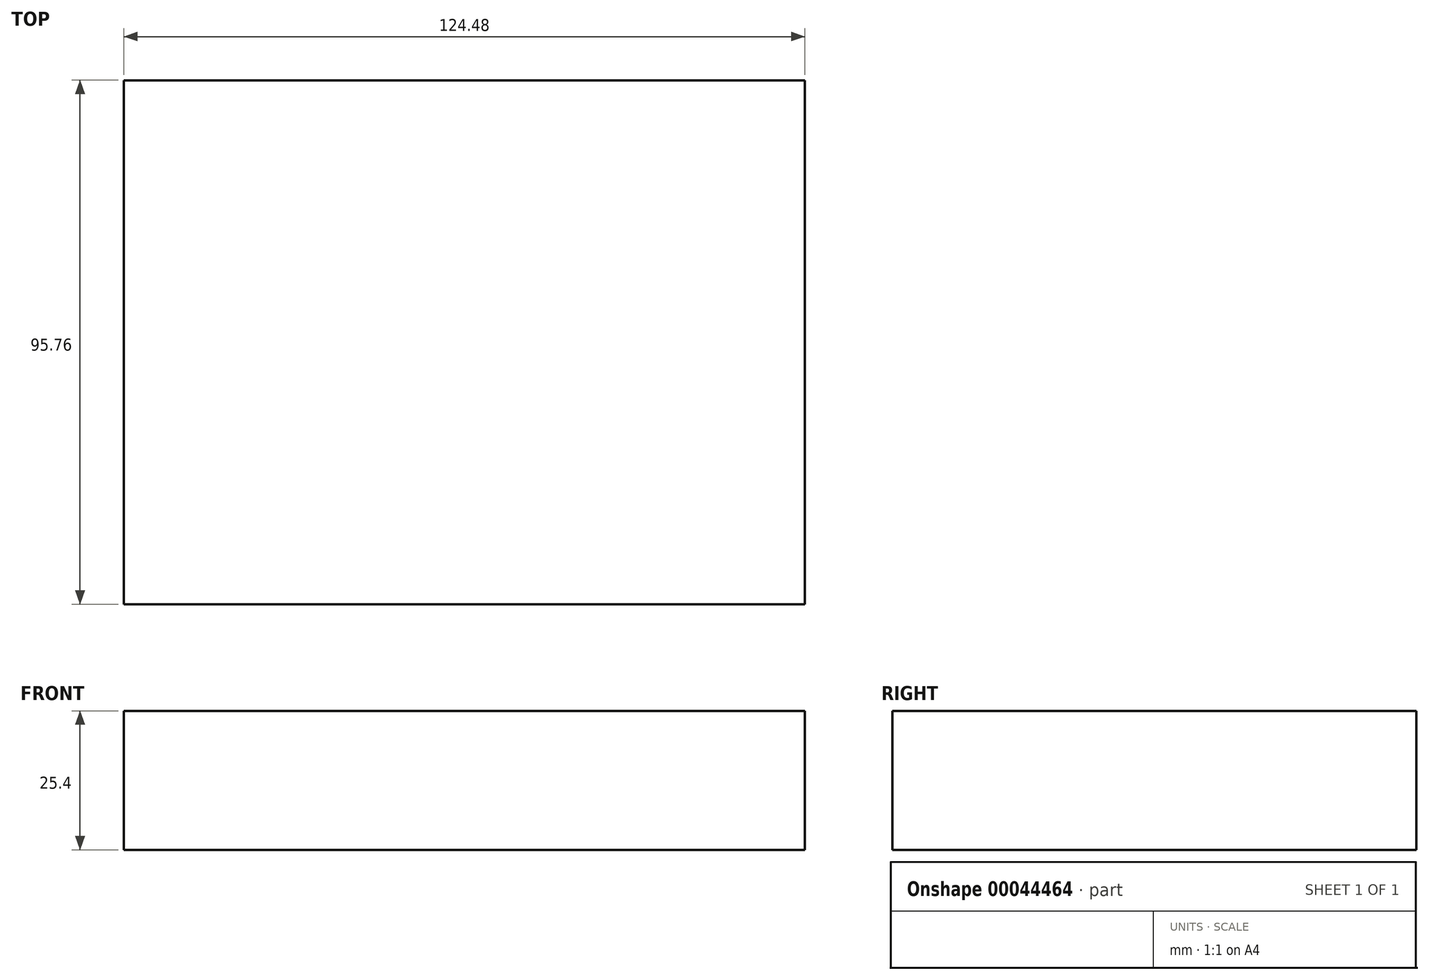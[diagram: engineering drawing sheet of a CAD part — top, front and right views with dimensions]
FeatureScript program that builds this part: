
annotation { "Feature Type Name" : "Feature", "Feature Type Description" : "" }
export const myFeature = defineFeature(function(context is Context, id is Id, definition is map)
    precondition{}
    {
        {
            var Q0;
            Q0=qCreatedBy(makeId("Top.planeOp"),FACE);
            var sketch = newSketch(context, id + "F0", { "sketchPlane" : qUnion([Q0])});
            skLineSegment(sketch, "E0.bottom", {"start": v(-58.16, 46.7) * mm, "end": v(66.32, 46.7) * mm});
            skLineSegment(sketch, "E0.top", {"start": v(-58.16, -49.06) * mm, "end": v(66.32, -49.06) * mm});
            skLineSegment(sketch, "E0.left", {"start": v(-58.16, 46.7) * mm, "end": v(-58.16, -49.06) * mm});
            skLineSegment(sketch, "E0.right", {"start": v(66.32, 46.7) * mm, "end": v(66.32, -49.06) * mm});
            skSolve(sketch);
        }
        {
            var Q0;
            Q0=makeQuery(id+"F0.imprint","IMPRINT",FACE,{"disambiguationData":[TD([[makeQuery(id+"F0.imprint","IMPRINT",EDGE,{"derivedFrom":sQuery(id+"F0.wireOp",EDGE,"E0.bottom")}),-1.0]])]});
            extrude(context, id + "F1", {"entities" : qUnion([Q0]), "depth" : 25.4 * mm});
        }
    });
